# Revit family: FAUCET (345)
name_source: partatom
category: Plumbing Fixtures
units: mm (PartAtom-declared; Revit-internal decimal feet)

## family parameters
Always vertical = Yes
Cut with Voids When Loaded = No
OmniClass Number = 23.45.00.00
OmniClass Title = Sanitary, Laundry, and Cleaning Equipment
Part Type = Normal
Room Calculation Point = No
Round Connector Dimension = Use Radius
Shared = No
Work Plane-Based = Yes

## types (1)
- Venetian Bronze
    Assembly Code = D2010400
    Connector Radius = 0' - 0 1/2"
    Default Elevation = 4' - 0"
    Description = Two Handle Floor Mount Freestanding Tub Filler
    Finish = Bronze-Brizo-Venetian Bronze
    Height = 0' - 8 3/4"
    Manufacturer = Brizo
    Model = T70338
    Product Documentation Link = https://www.brizo.com
    Product Name = Tresa™ Collection
    Style = Tub Filler
    Type Comments = Wall Mount
    URL = http://www.brizo.com
    Width = 0' - 8"

## geometry (parser evidence)
native form markers: Blend x4, Sweep x6
no freeform markers — native parametric forms only
